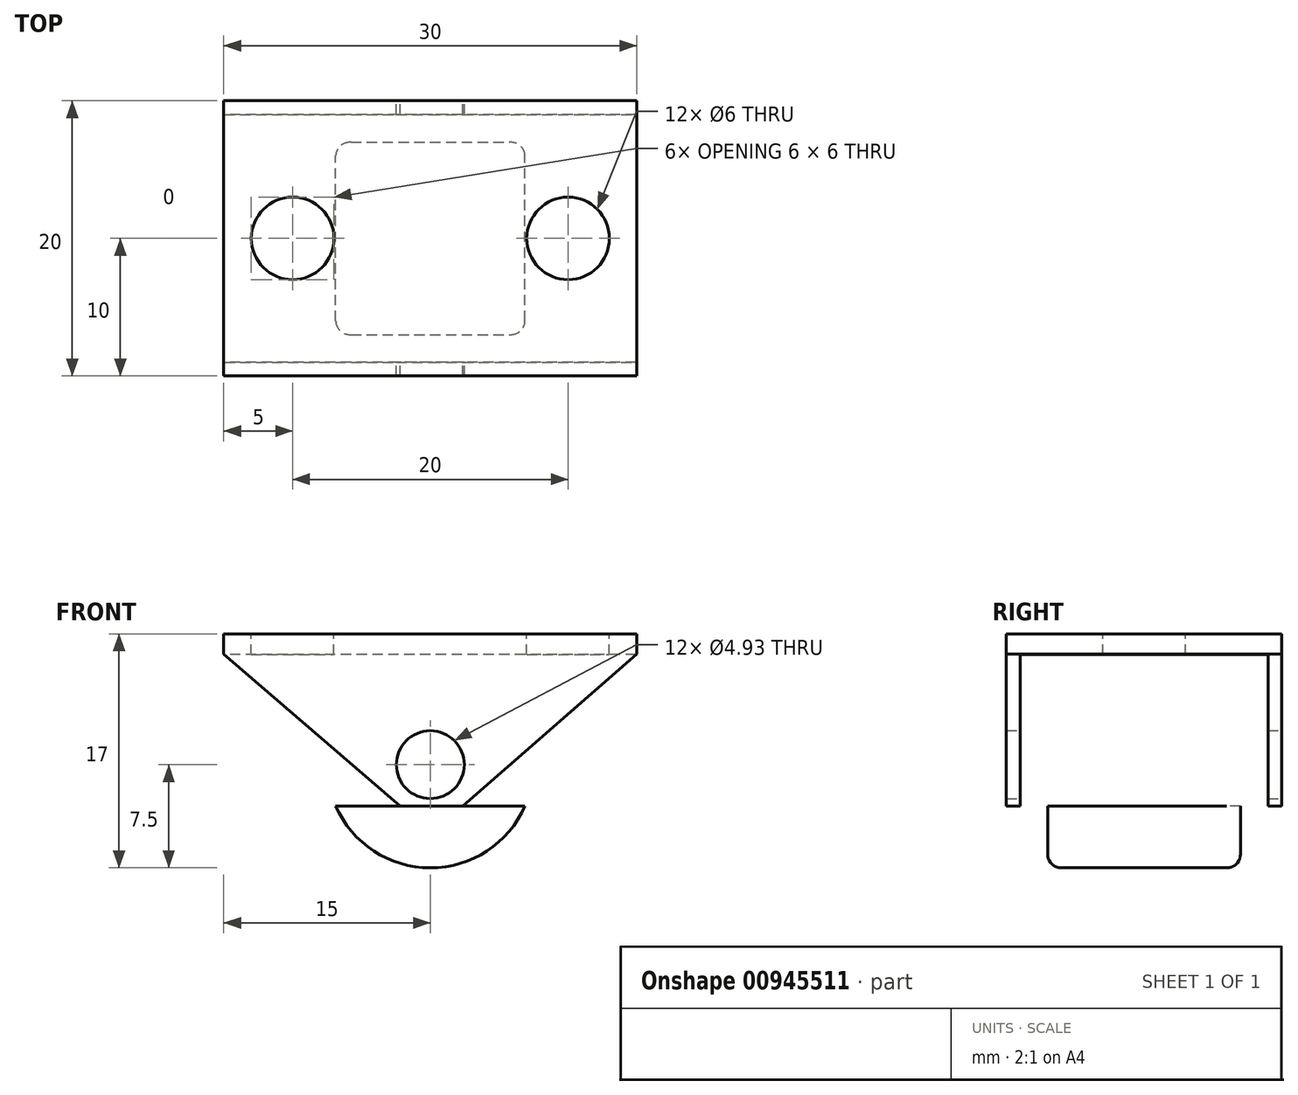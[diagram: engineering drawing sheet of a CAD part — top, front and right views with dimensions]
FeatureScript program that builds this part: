
annotation { "Feature Type Name" : "Feature", "Feature Type Description" : "" }
export const myFeature = defineFeature(function(context is Context, id is Id, definition is map)
    precondition{}
    {
        {
            var Q0;
            Q0=qCreatedBy(makeId("Front.planeOp"),FACE);
            var sketch = newSketch(context, id + "F0", { "sketchPlane" : qUnion([Q0])});
            skCircle(sketch, "E0", {"center": v(0, 0) * mm, "radius": 7.5 * mm});
            skCircle(sketch, "E1", {"center": v(0, 0) * mm, "radius": 2.5 * mm});
            skSolve(sketch);
        }
        {
            var Q0;
            Q0=makeQuery(id+"F0.imprint","IMPRINT",FACE,{"disambiguationData":[TD([[makeQuery(id+"F0.imprint","IMPRINT",EDGE,{"derivedFrom":sQuery(id+"F0.wireOp",EDGE,"E0")}),1.0]])]});
            extrude(context, id + "F1", {"entities" : qUnion([Q0]), "endBound" : BoundingType.SYMMETRIC, "depth" : 14 * mm, "offsetDistance" : 25 * mm});
        }
        {
            var Q0;
            Q0=makeQuery(id+"F1.opExtrude","CAP_EDGE",EDGE,{"disambiguationData":[OSD([sQuery(id+"F0.wireOp",EDGE,"E0")])],"isStart":false});
            var Q1;
            Q1=makeQuery(id+"F1.opExtrude","CAP_EDGE",EDGE,{"disambiguationData":[OSD([sQuery(id+"F0.wireOp",EDGE,"E0")])],"isStart":true});
            fillet(context, id + "F2", {"entities" : qUnion([Q0, Q1]), "radius" : 1 * mm, "tangentPropagation" : true, "allowEdgeOverflow" : false});
        }
        {
            var Q0;
            Q0=qCreatedBy(makeId("Front.planeOp"),FACE);
            var sketch = newSketch(context, id + "F3", { "sketchPlane" : qUnion([Q0])});
            skLineSegment(sketch, "E2", {"start": v(2.36, -3) * mm, "end": v(15, 8.05) * mm});
            skLineSegment(sketch, "E3", {"start": v(15, 8.05) * mm, "end": v(15, 9.5) * mm});
            skLineSegment(sketch, "E4", {"start": v(15, 9.5) * mm, "end": v(-15, 9.5) * mm});
            skLineSegment(sketch, "E5", {"start": v(-15, 9.5) * mm, "end": v(-15, 8.05) * mm});
            skLineSegment(sketch, "E6", {"start": v(-15, 8.05) * mm, "end": v(-2.2, -3) * mm});
            skLineSegment(sketch, "E7", {"start": v(-2.2, -3) * mm, "end": v(2.36, -3) * mm});
            skCircle(sketch, "E8", {"center": v(0, 0) * mm, "radius": 2.47 * mm});
            skSolve(sketch);
        }
        {
            var Q0;
            Q0 = qSketchRegion(id + "F3", true);
            extrude(context, id + "F4", {"entities" : qUnion([Q0]), "endBound" : BoundingType.SYMMETRIC, "depth" : 20 * mm, "offsetDistance" : 25 * mm});
        }
        {
            var Q0;
            Q0=makeQuery(id+"F4.opExtrude","SWEPT_FACE",FACE,{"disambiguationData":[OSD([sQuery(id+"F3.wireOp",EDGE,"E7")])]});
            var sketch = newSketch(context, id + "F5", { "sketchPlane" : qUnion([Q0])});
            skLineSegment(sketch, "E9.bottom", {"start": v(16.2, -9) * mm, "end": v(-16.2, -9) * mm});
            skLineSegment(sketch, "E9.top", {"start": v(16.2, 9) * mm, "end": v(-16.2, 9) * mm});
            skLineSegment(sketch, "E9.left", {"start": v(16.2, -9) * mm, "end": v(16.2, 9) * mm});
            skLineSegment(sketch, "E9.right", {"start": v(-16.2, -9) * mm, "end": v(-16.2, 9) * mm});
            skPoint(sketch, "E9.middle", {"position": v(0, 0) * mm});
            skSolve(sketch);
        }
        {
            var Q0;
            Q0 = qSketchRegion(id + "F5", true);
            extrude(context, id + "F6", {"entities" : qUnion([Q0]), "operationType" : NewBodyOperationType.REMOVE, "oppositeDirection" : true, "depth" : 11 * mm, "offsetDistance" : 25 * mm});
        }
        {
            var Q0;
            Q0=makeQuery(id+"F4.opExtrude","SWEPT_FACE",FACE,{"disambiguationData":[OSD([sQuery(id+"F3.wireOp",EDGE,"E4")])]});
            var sketch = newSketch(context, id + "F7", { "sketchPlane" : qUnion([Q0])});
            skCircle(sketch, "E10", {"center": v(10, 0) * mm, "radius": 3 * mm});
            skCircle(sketch, "E11", {"center": v(-10, 0) * mm, "radius": 3 * mm});
            skSolve(sketch);
        }
        {
            var Q0;
            Q0=makeQuery(id+"F7.imprint","IMPRINT",FACE,{"disambiguationData":[TD([[makeQuery(id+"F7.imprint","IMPRINT",EDGE,{"derivedFrom":sQuery(id+"F7.wireOp",EDGE,"E11")}),1.0]])]});
            var Q1;
            Q1=makeQuery(id+"F7.imprint","IMPRINT",FACE,{"disambiguationData":[TD([[makeQuery(id+"F7.imprint","IMPRINT",EDGE,{"derivedFrom":sQuery(id+"F7.wireOp",EDGE,"E10")}),1.0]])]});
            extrude(context, id + "F8", {"entities" : qUnion([Q0, Q1]), "operationType" : NewBodyOperationType.REMOVE, "oppositeDirection" : true, "depth" : 2 * mm, "offsetDistance" : 25 * mm});
        }
    });
